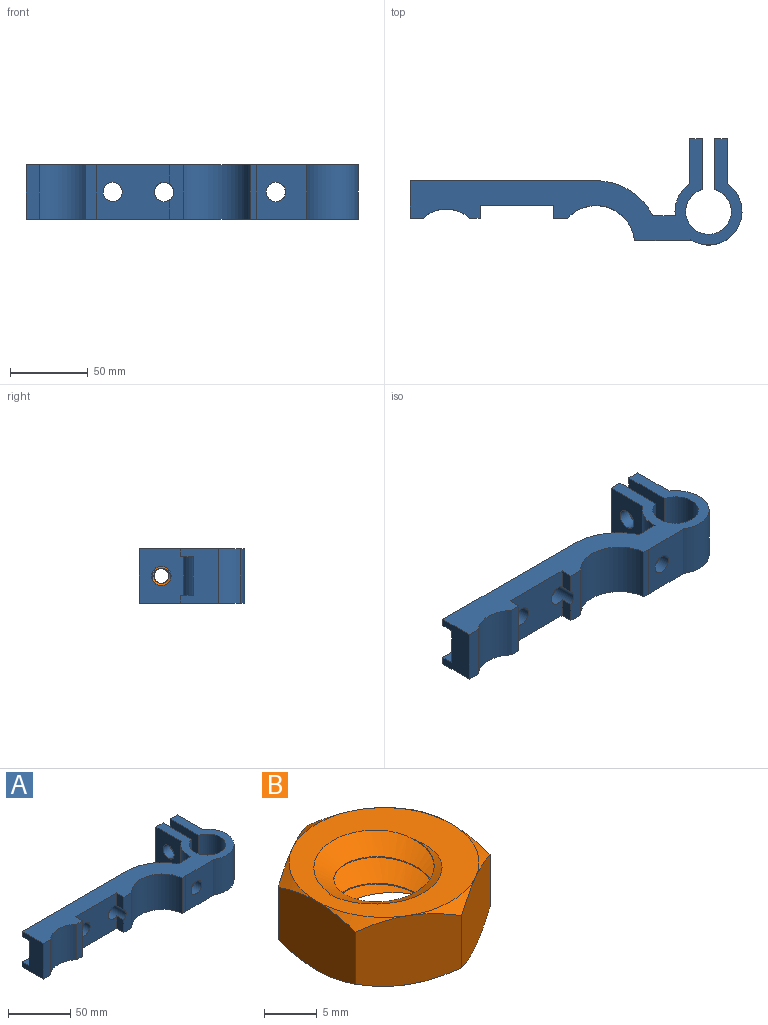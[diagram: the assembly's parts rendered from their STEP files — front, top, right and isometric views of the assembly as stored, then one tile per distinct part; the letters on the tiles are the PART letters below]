
ASSEMBLY  parts=2 mates=1
PART A: 47 faces, bbox 213x68x35 mm
  f0: plane 212.99x68.02mm, normal (0,0,1), area 4446.8mm2, adj f1,f3,f4,f5,f7,f8,f9,f10
  f1: cylinder r=21.5mm len=35mm, axis (0,0,-1), area 1039.1mm2, adj f0,f2,f16,f17,f21,f27,f28,f39
  f2: plane 25x22.33mm, normal (-0.01,1,0), area 439.5mm2, adj f1,f16,f17,f18,f29
  f3: plane 35x4.04mm, normal (0,-1,0), area 141.5mm2, adj f0,f21,f22,f26
  f4: plane 12.5x8mm, normal (-1,0,0), area 100mm2, adj f0,f5,f7,f23
  f5: plane 35x9mm, normal (0,-1,0), area 297mm2, adj f0,f4,f6,f21,f22,f23
  f6: plane 12.5x8mm, normal (-1,0,0), area 100mm2, adj f5,f7,f21,f23
  f7: plane 47.13x35mm, normal (0,-1,0), area 1429.9mm2, adj f0,f4,f6,f8,f21,f23,f24
  f8: plane 35x8mm, normal (1,0,0), area 280mm2, adj f0,f7,f9,f21
  f9: plane 35x6.8mm, normal (0,-1,0), area 237.9mm2, adj f0,f8,f10,f21
  f10: cylinder r=22.2mm len=35mm, axis (0,0,1), area 1146.4mm2, adj f0,f9,f11,f21
  f11: plane 35x8.34mm, normal (0,-1,0), area 292mm2, adj f0,f10,f14,f21
  f12: plane 119.35x5mm, normal (0,1,0), area 596.7mm2, adj f0,f14,f17,f20
  f13: plane 119.35x25mm, normal (0,1,0), area 2746.1mm2, adj f14,f16,f17,f18,f23,f24
  f14: plane 35x24mm, normal (-1,0,0), area 640mm2, adj f0,f11,f12,f13,f15,f16,f17,f21
  f15: plane 119.35x5mm, normal (0,1,0), area 596.7mm2, adj f14,f16,f19,f21
  f16: plane 172.78x30.5mm, normal (0,0,1), area 1443.2mm2, adj f1,f2,f13,f14,f15,f18,f19,f28
  f17: plane 172.78x30.5mm, normal (0,0,-1), area 1443.2mm2, adj f1,f2,f12,f13,f14,f18,f20,f27
  f18: cylinder r=32.74mm len=31.1mm, axis (0,0,1), area 1025.2mm2, adj f2,f13,f16,f17
  f19: cylinder r=40.74mm len=36.41mm, axis (0,0,1), area 225.2mm2, adj f15,f16,f21,f28
  f20: cylinder r=40.74mm len=36.41mm, axis (0,0,1), area 225.2mm2, adj f0,f12,f17,f27
  f21: plane 212.99x68.02mm, normal (0,0,-1), area 4446.8mm2, adj f1,f3,f5,f6,f7,f8,f9,f10
  f22: cylinder r=24.74mm len=42.85mm, axis (0,0,1), area 1995.5mm2, adj f0,f3,f5,f21
  f23: cylinder r=6.15mm len=16mm, axis (0,-1,0), area 402.5mm2, adj f4,f5,f6,f7,f13
  f24: cylinder r=6.15mm len=12.3mm, axis (0,-1,0), area 309.1mm2, adj f7,f13
  f25: plane 35x32mm, normal (0.01,-1,0), area 1001.2mm2, adj f0,f21,f26,f29,f32
  f26: plane 35x0.09mm, normal (-1,-0.01,0), area 3.3mm2, adj f0,f3,f21,f25
  f27: plane 14.4x5mm, normal (-0.01,1,0), area 72mm2, adj f0,f1,f17,f20
  f28: plane 14.4x5mm, normal (-0.01,1,0), area 72mm2, adj f1,f16,f19,f21
  f29: cylinder r=6.15mm len=12.36mm, axis (-0.01,1,0), area 309.1mm2, adj f2,f25
  f30: cylinder r=14.64mm len=35mm, axis (0,0,-1), area 2935.5mm2, adj f0,f21,f33,f34,f35,f36,f37,f38
  f31: cylinder r=21.5mm len=39.34mm, axis (0,0,-1), area 2342mm2, adj f0,f21,f32,f44
  f32: plane 35x0.34mm, normal (1,0.01,0), area 12mm2, adj f0,f21,f25,f31
  f33: plane 5x0.12mm, normal (1,0.01,0), area 0.6mm2, adj f0,f30,f34,f35
  f34: plane 0.12x0.09mm, normal (0,0,-1), area 0mm2, adj f30,f33,f35
  f35: plane 5x0.09mm, normal (-0.01,1,0), area 0.4mm2, adj f0,f30,f33,f34
  f36: plane 5x0.09mm, normal (-0.01,1,0), area 0.4mm2, adj f21,f30,f37,f38
  f37: plane 0.12x0.09mm, normal (0,0,1), area 0mm2, adj f30,f36,f38
  f38: plane 5x0.12mm, normal (1,0.01,0), area 0.6mm2, adj f21,f30,f36,f37
  f39: plane 35x28.68mm, normal (-1,0,0), area 881.1mm2, adj f0,f1,f21,f40,f46
  f40: plane 35x8mm, normal (0,1,0), area 280mm2, adj f0,f21,f39,f41
  f41: plane 35x32.43mm, normal (1,0,0), area 1012.4mm2, adj f0,f21,f30,f40,f46
  f42: plane 35x32.43mm, normal (-1,0,0), area 1012.4mm2, adj f0,f21,f30,f43,f45
  f43: plane 35x8mm, normal (0,1,0), area 280mm2, adj f0,f21,f42,f44
  f44: plane 35x28.68mm, normal (1,0,0), area 881.1mm2, adj f0,f21,f31,f43,f45
  f45: cylinder r=6.25mm len=12.5mm, axis (1,0,0), area 314.2mm2, adj f42,f44
  f46: cylinder r=6.25mm len=12.5mm, axis (1,0,0), area 314.2mm2, adj f39,f41
PART B: 23 faces, bbox 22.8x22.8x13.9 mm
  f0: cylinder r=4.75mm len=9.5mm, axis (0,0,-1), area 7.5mm2, adj f1,f2,f21,f22
  f1: plane 20.02x20.02mm, normal (0,0,1), area 139.2mm2, adj f0,f5,f6,f8,f10,f12,f14,f21
  f2: plane 20.06x20.06mm, normal (0,0,-1), area 139.2mm2, adj f0,f3,f4,f7,f9,f11,f13,f21
  f3: cone r=14.27mm half-angle=55deg, axis (0,0,1), area 8.4mm2, adj f2,f15,f20
  f4: cone r=14.27mm half-angle=55deg, axis (0,0,1), area 8.4mm2, adj f2,f15,f16
  f5: cone r=14.27mm half-angle=55deg, axis (0,0,-1), area 8.4mm2, adj f1,f15,f20
  f6: cone r=14.27mm half-angle=55deg, axis (0,0,-1), area 8.4mm2, adj f1,f15,f16
  f7: cone r=14.27mm half-angle=55deg, axis (0,0,1), area 8.4mm2, adj f2,f16,f17
  f8: cone r=14.27mm half-angle=55deg, axis (0,0,-1), area 8.4mm2, adj f1,f16,f17
  f9: cone r=14.27mm half-angle=55deg, axis (0,0,1), area 8.4mm2, adj f2,f17,f18
  f10: cone r=14.27mm half-angle=55deg, axis (0,0,-1), area 8.4mm2, adj f1,f17,f18
  f11: cone r=14.27mm half-angle=55deg, axis (0,0,1), area 8.4mm2, adj f2,f18,f19
  f12: cone r=14.27mm half-angle=55deg, axis (0,0,-1), area 8.4mm2, adj f1,f18,f19
  f13: cone r=14.27mm half-angle=55deg, axis (0,0,1), area 8.4mm2, adj f2,f19,f20
  f14: cone r=14.27mm half-angle=55deg, axis (0,0,-1), area 8.4mm2, adj f1,f19,f20
  f15: plane 11.29x8.9mm, normal (-1,0,0), area 76.2mm2, adj f3,f4,f5,f6,f16,f20
  f16: plane 9.9x8.91mm, normal (-0.5,0.87,0), area 76.2mm2, adj f4,f6,f7,f8,f15,f17
  f17: plane 9.9x8.91mm, normal (0.5,0.87,0), area 76.2mm2, adj f7,f8,f9,f10,f16,f18
  f18: plane 11.29x8.9mm, normal (1,0,0), area 76.2mm2, adj f9,f10,f11,f12,f17,f19
  f19: plane 9.9x8.91mm, normal (0.5,-0.87,0), area 76.2mm2, adj f11,f12,f13,f14,f18,f20
  f20: plane 9.9x8.91mm, normal (-0.5,-0.87,0), area 76.2mm2, adj f3,f5,f13,f14,f15,f19
  f21: bspline ~16.97x14.7mm, area 295.4mm2, adj f0,f1,f2,f22
  f22: bspline ~16.97x14.7mm, area 295.2mm2, adj f0,f1,f2,f21
PLACE A t=(84.12,-94.46,-47.43)mm
PLACE B rot(axis=(0,-1,0),90deg) t=(50.82,-41.6,5.07)mm
MATE fastened A.f45 <-> B.f3  axis (-1,0,0) through (42.82,-41.6,5.07)mm
